# Revit family: Urinal_Electrical-Wall_Mount-KOHLER-MODERN_LIFE-K-21841T-1
name_source: partatom
category: Plumbing Fixtures
revit_build: Autodesk Revit 2017 (Build: 20160225_1515(x64)
units: mm (PartAtom-declared; Revit-internal decimal feet)

## family parameters
Cut with Voids When Loaded = No
Host = Face
OmniClass Number = 23.31.21.00
Part Type = Normal
Room Calculation Point = No
Round Connector Dimension = Use Diameter
Shared = No

## types (3) — shared parameters
ADA Compliant = No
Apparent Load = 0 VA
Assembly Code = D2010200
CW Connection = Yes
Cold Water Inlet = Cold Water Inlet
Date Modified = 05/11/2021
Default Elevation = 0"
Electrical Connector = Yes
Electrical Note = One Dedicated Circuit Required
Finish = Kohler-Vitreous_China-0-White
Flow Rate = 0 GPM
HW Connection = No
Height = 27 7/16"
Hot Water Inlet = Hot Water Inlet
Length = 13 1/2"
Manufacturer = KOHLER Co.
Master Format 2014 = 22 41 13.16
Master Format 2014 Name = Residential Urinals
Material = Vitreous China
Pressure = 79.77 psi
Product Documentation Link = https://files.kohler.com.cn
Product Name = MODERN LIFE
Product Page URL = https://www.kohler.com.cn
URL = http://www.kohler.com.cn
Vent Connection = No
Voltage = 220 V
Waste Connection = Yes
Waste Water Outlet = Waste Water Outlet
WaterSense Certified = No
Width = 12 1/16"

## per-type parameters (varying)
| type | Description | Flush Rate- GPF | Flush Rate- LPF | Model | Type |
| 2.5 L, 0-White | Minglai wall-mounted automatic sensor urinal (AC) (2.5L) | 0.67 GPF | 2.5 LPF | K-21841T-C05-0 | 1 |
| Electrolyzed Water,2.5 L, 0-White | Minglai wall-mounted sterilization automatic sensor urinal (AC) (2.5L) | 0.67 GPF | 2.5 LPF | K-21841T-EW-0 | 2 |
| Water-Saving Electrolyzed Water,1 L, 0-White | Minglai wall-mounted water-saving automatic sterilization urinal (AC) (1L) | 0.26 GPF | 1 LPF | K-21841T-WEW-0 | 3 |

## geometry (parser evidence)
native form markers: Sweep x5
no freeform markers — native parametric forms only
